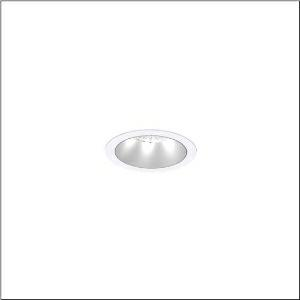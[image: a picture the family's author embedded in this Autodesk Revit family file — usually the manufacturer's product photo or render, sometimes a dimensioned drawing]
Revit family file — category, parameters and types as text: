
# Revit family: lunis_21_m_51db19ec91c
name_source: partatom
category: Lighting Fixtures
units: mm (PartAtom-declared; Revit-internal decimal feet)

## family parameters
Cut with Voids When Loaded = No
Host = Face
Light Source = No
Part Type = Normal
Room Calculation Point = No
Round Connector Dimension = Use Diameter
Shared = No

## types (1)
- --- (1 x LED, 3720 lm, 25.5 W, 6500K)
    Apparent Load = 26 VA
    CIE Flux Codes = 93 99 100 100 100
    Color Rendering = 80
    Color Temperature = 6500K
    Default Elevation = 1800 mm
    Description = Lunis 21,  M, downlight, light control with lens, of PMMA, anti glare with reflector, of PC, matt, light emission: direct distribution, LED rated luminous flux: 1.730lm, light colour: 830/840/865, with terminal, 5-pole, mains connection: 220..240V, AC/DC, 0/50..60Hz, housing, round, of diecast aluminium, traffic white (RAL 9016), diameter: 115mm, clamping range: 1..40mm, protection rating (complete): IP20, protection rating (on room side): IP54, insulation class (complete): insulation class II (safety insulation), certification: CE, impact resistance: IK03, packaging unit: 1 piece
    Height = 0 mm  [stored 0 ft]
    Lamp = 1 x LED
    Lamp Light Flux = 3720 lm
    Lamp Power = 25.5 W
    Lamp count = 1
    Length = 115 mm
    Luminous efficacy = 146 lm/W
    Manufacturer = Siteco
    ModVariant = No
    Model = 51DB19EC91C
    Mounting Place = Ceiling
    Mounting Type = Recessed
    Number of Poles = 1
    OnlyDefault = Yes
    Power Factor = 1
    Product Name = Lunis 21 M
    Product group = downlight
    ProductGroupID = 400
    Protection Class = Protection class II
    Protection Degree = IP 20
    RLX_Detail_Level = 1
    RLX_Emergency_Light_Flux = 0 lm
    RLX_Emergency_Type = 0
    RLX_Emergency_Type_DB = No
    RlxData = <blob elided: 14945 chars, md5=d63a65a7>
    Socket = socket
    Standby Power = 0 W
    System Light Flux = 3720 lm
    System Power = 26 W
    Type Comments = individual setting: colour temperature 6500K, luminous flux: 100 % | (ON | ON | OFF | OFF) | 700 mA
    Type Image = l_1290856.jpg
    URL = http://relux.com
    VarID = @adj_019022
    Voltage = 0 V
    Weight = 0.00 kg
    Width = 0 mm  [stored 0 ft]

note: [stored X ft] marks values corroborated as IEEE doubles in the binary element streams (Revit-internal decimal feet)

## geometry (parser evidence)
native form markers: Sweep x10
no freeform markers — native parametric forms only
